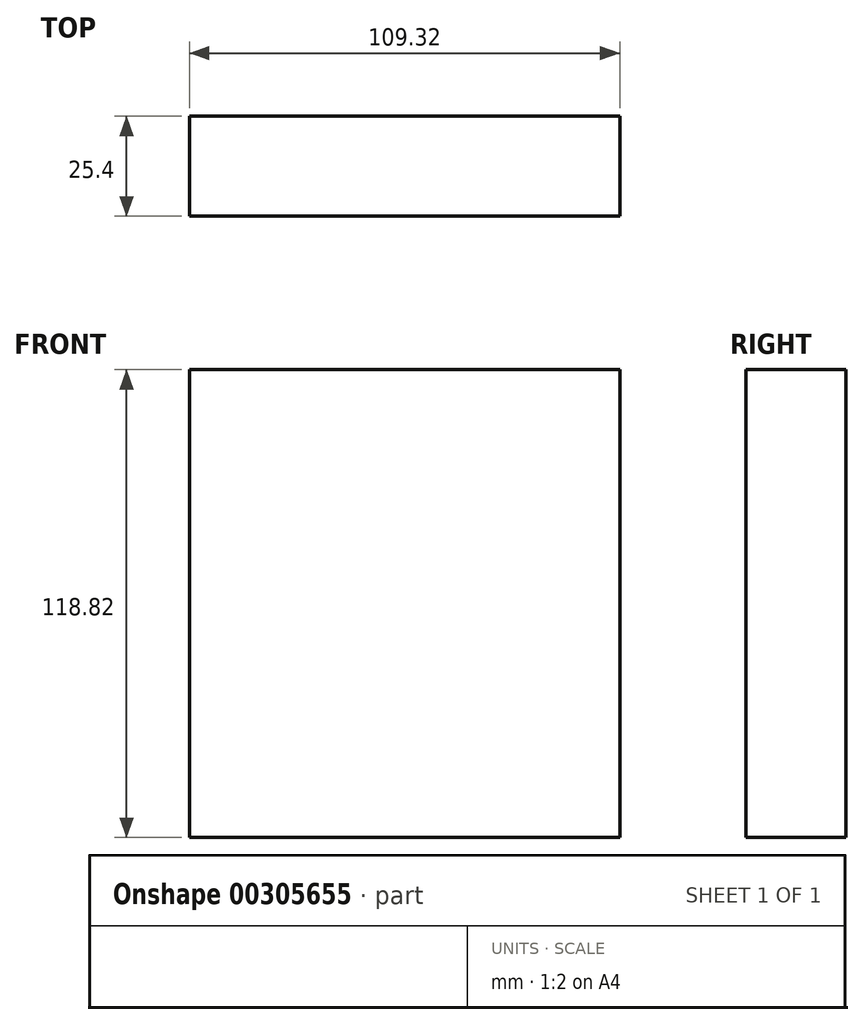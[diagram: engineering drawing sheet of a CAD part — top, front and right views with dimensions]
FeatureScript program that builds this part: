
annotation { "Feature Type Name" : "Feature", "Feature Type Description" : "" }
export const myFeature = defineFeature(function(context is Context, id is Id, definition is map)
    precondition{}
    {
        {
            var Q0;
            Q0=qCreatedBy(makeId("Front.planeOp"),FACE);
            var sketch = newSketch(context, id + "F0", { "sketchPlane" : qUnion([Q0])});
            skLineSegment(sketch, "E0.bottom", {"start": v(-150.3, 95.15) * mm, "end": v(11.31, 95.15) * mm});
            skLineSegment(sketch, "E0.top", {"start": v(-150.3, -23.67) * mm, "end": v(11.31, -23.67) * mm});
            skLineSegment(sketch, "E0.left", {"start": v(-150.3, 95.15) * mm, "end": v(-150.3, -23.67) * mm});
            skLineSegment(sketch, "E0.right", {"start": v(11.31, 95.15) * mm, "end": v(11.31, -23.67) * mm});
            skLineSegment(sketch, "E1.bottom", {"start": v(-40.97, 164.87) * mm, "end": v(119.05, 164.87) * mm});
            skLineSegment(sketch, "E1.top", {"start": v(-40.97, -129.82) * mm, "end": v(119.05, -129.82) * mm});
            skLineSegment(sketch, "E1.left", {"start": v(-40.97, 164.87) * mm, "end": v(-40.97, -129.82) * mm});
            skLineSegment(sketch, "E1.right", {"start": v(119.05, 164.87) * mm, "end": v(119.05, -129.82) * mm});
            skSolve(sketch);
        }
        {
            var Q0;
            {var subQ0=sQuery(id+"F0.wireOp",EDGE,"E0.left");Q0=makeQuery(id+"F0.imprint","IMPRINT",FACE,{"disambiguationData":[TD([[makeQuery(id+"F0.imprint","IMPRINT",EDGE,{"derivedFrom":subQ0}),1.0]])]});}
            extrude(context, id + "F1", {"entities" : qUnion([Q0]), "depth" : 25.4 * mm});
        }
    });
